# Revit family: SonoSensor30_DN15-DN20_RFA
name_source: partatom
category: Pipe Accessories
revit_build: Autodesk Revit 2017 (Build: 20161205_1400(x64)
units: mm (PartAtom-declared; Revit-internal decimal feet)

## family parameters
Always vertical = Yes
Cut with Voids When Loaded = No
Part Type = Valve - Breaks Into
Round Connector Dimension = Use Diameter
Shared = No
Work Plane-Based = No

## types (3) — shared parameters
A = 45.00°
Body Material = Danfoss Brass
Description = Flow Meter
H = 67 mm  [stored 0.219816 ft]
H1 = 28 mm  [stored 0.0918635 ft]
IfcExportAs = IfcValveType
IfcExportType = SonoSensor30
LOD 200 = No
LOD 350 = Yes
Lnut = 13 mm
Manufacturer = Danfoss
Model = SonoSensor30
Operation Pressure = PN16
URL = https://store.danfoss.com

## per-type parameters (varying)
| type | A_H | D | D1 | D2 | D3 | D4 | D5 | L | L-1 | L1 | L1-1 | L10 | L2 | L2-1 | L3 | L4 | L5 | L6 | L7 | L8 | L9 | Max Flow | Nominal Flow | Weight |
| SonoSensor30_DN15_G3/4_110mm | 41 mm | 15 mm  [stored 0.0492126 ft] | 25 mm  [stored 0.082021 ft] | 26 mm | 21 mm  [stored 0.0688976 ft] | 19 mm | 31 mm  [stored 0.101706 ft] | 110 mm  [stored 0.360892 ft] | 10 mm  [stored 0.0328084 ft] | 122 mm | 16 mm | 49 mm  [stored 0.160761 ft] | 188 mm | 49 mm  [stored 0.160761 ft] | 49 mm  [stored 0.160761 ft] | 14 mm  [stored 0.0459318 ft] | 15 mm  [stored 0.0492126 ft] | 8 mm  [stored 0.0262467 ft] | 76 mm | 9 mm  [stored 0.0295276 ft] | 81 mm  [stored 0.265748 ft] | 1.2m3/h, 3.0m3/h | 0.6m3/h, 1.5m3/h | 0.80 kg |
| SonoSensor30_DN20_G1_130mm | 43 mm | 20 mm  [stored 0.0656168 ft] | 30 mm  [stored 0.0984252 ft] | 33 mm | 26 mm | 24 mm  [stored 0.0787402 ft] | 36 mm  [stored 0.11811 ft] | 130 mm | 6 mm  [stored 0.019685 ft] | 145 mm | 14 mm  [stored 0.0459318 ft] | 61 mm | 222 mm | 52 mm  [stored 0.170604 ft] | 61 mm | 15 mm  [stored 0.0492126 ft] | 17 mm | 9 mm  [stored 0.0295276 ft] | 96 mm | 10 mm  [stored 0.0328084 ft] | 77 mm | 5.0m3/h | 2.5 m3/h | 0.90 kg |
| SonoSensor30_DN20_G1_190mm | 43 mm | 20 mm  [stored 0.0656168 ft] | 31 mm  [stored 0.101706 ft] | 33 mm | 26 mm | 24 mm  [stored 0.0787402 ft] | 36 mm  [stored 0.11811 ft] | 190 mm | 11 mm  [stored 0.0360892 ft] | 205 mm | 19 mm | 103 mm | 282 mm | 57 mm | 84 mm | 17 mm | 17 mm | 9 mm  [stored 0.0295276 ft] | 147 mm | 10 mm  [stored 0.0328084 ft] | 130 mm | 5.0m3/h | 2.5 m3/h | 1.00 kg |

note: column(s) folded — value = type name in every type: Model Type

note: [stored X ft] marks values corroborated as IEEE doubles in the binary element streams (Revit-internal decimal feet)

## geometry (parser evidence)
native form markers: Sweep x9
no freeform markers — native parametric forms only
